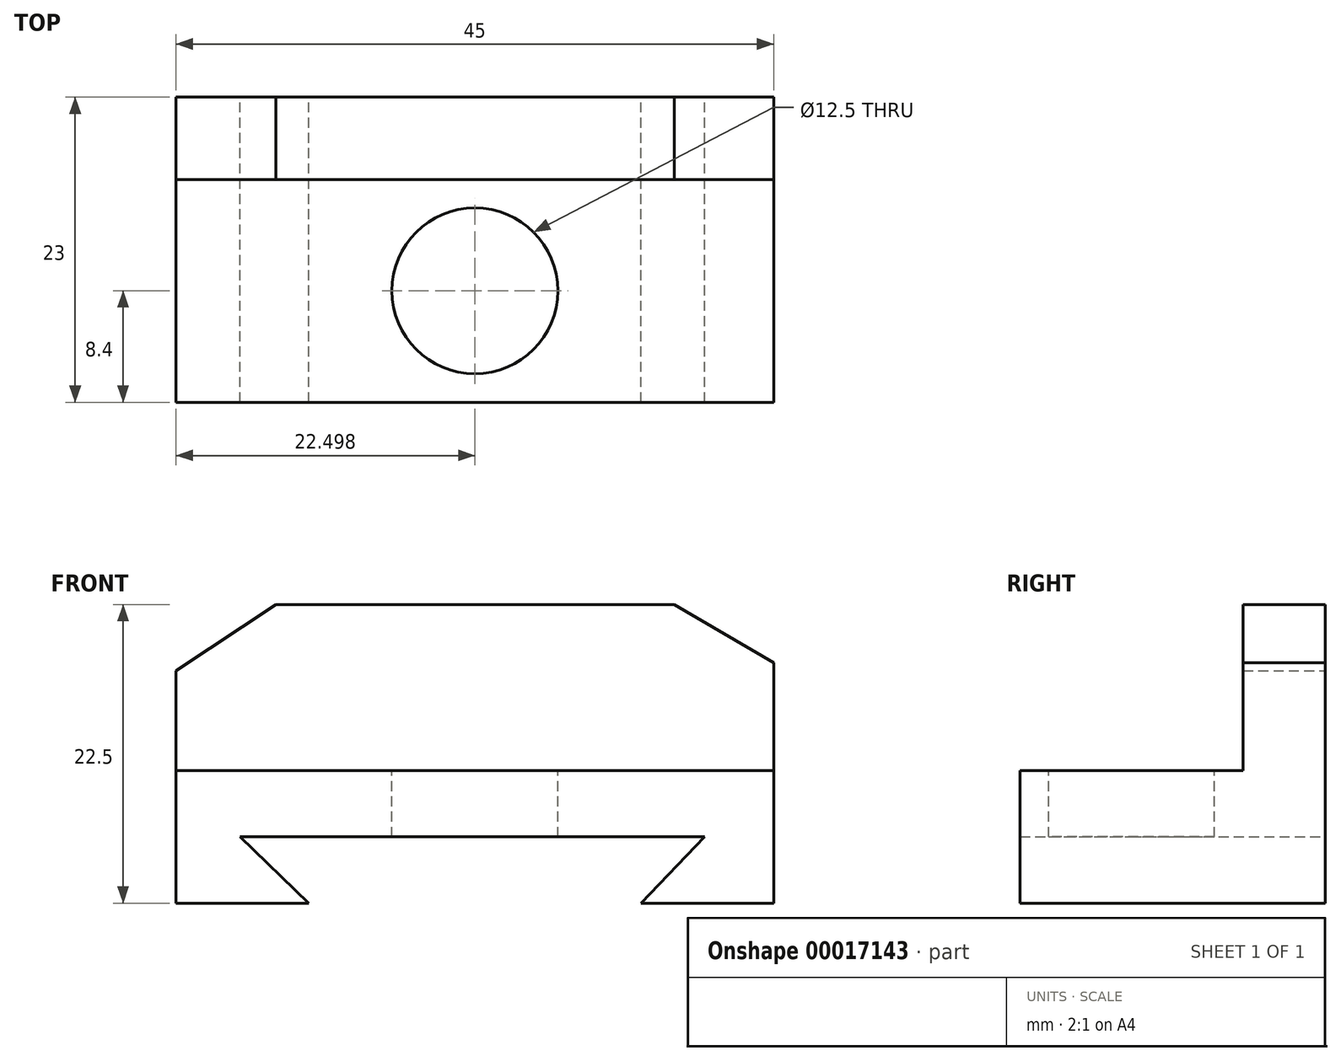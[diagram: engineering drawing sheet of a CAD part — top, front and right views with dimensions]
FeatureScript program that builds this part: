
annotation { "Feature Type Name" : "Feature", "Feature Type Description" : "" }
export const myFeature = defineFeature(function(context is Context, id is Id, definition is map)
    precondition{}
    {
        {
            var Q0;
            Q0=qCreatedBy(makeId("Front.planeOp"),FACE);
            var sketch = newSketch(context, id + "F0", { "sketchPlane" : qUnion([Q0])});
            skLineSegment(sketch, "E0", {"start": v(-23.08, -34) * mm, "end": v(-23.08, -24) * mm});
            skLineSegment(sketch, "E1", {"start": v(-23.08, -24) * mm, "end": v(-23.08, -16.5) * mm});
            skLineSegment(sketch, "E2", {"start": v(-23.08, -16.5) * mm, "end": v(-15.58, -11.5) * mm});
            skLineSegment(sketch, "E3", {"start": v(-15.58, -11.5) * mm, "end": v(14.42, -11.5) * mm});
            skLineSegment(sketch, "E4", {"start": v(21.92, -34) * mm, "end": v(21.92, -24) * mm});
            skLineSegment(sketch, "E5", {"start": v(21.92, -24) * mm, "end": v(21.92, -15.9) * mm});
            skLineSegment(sketch, "E6", {"start": v(-23.08, -24) * mm, "end": v(21.92, -24) * mm});
            skLineSegment(sketch, "E7", {"start": v(14.42, -11.5) * mm, "end": v(21.92, -15.9) * mm});
            skLineSegment(sketch, "E8", {"start": v(-23.08, -34) * mm, "end": v(-13.08, -34) * mm});
            skLineSegment(sketch, "E9", {"start": v(21.92, -34) * mm, "end": v(11.92, -34) * mm});
            skLineSegment(sketch, "E10", {"start": v(-13.08, -34) * mm, "end": v(-18.27, -29.01) * mm});
            skLineSegment(sketch, "E11", {"start": v(-18.27, -29.01) * mm, "end": v(16.73, -29.01) * mm});
            skLineSegment(sketch, "E12", {"start": v(11.92, -34) * mm, "end": v(16.73, -29.01) * mm});
            skSolve(sketch);
        }
        {
            var Q0;
            Q0=makeQuery(id+"F0.imprint","IMPRINT",FACE,{"disambiguationData":[TD([[makeQuery(id+"F0.imprint","IMPRINT",EDGE,{"derivedFrom":sQuery(id+"F0.wireOp",EDGE,"E0")}),-1.0]])]});
            extrude(context, id + "F1", {"entities" : qUnion([Q0]), "depth" : 23 * mm});
        }
        {
            var Q0;
            Q0 = qSketchRegion(id + "F0", true);
            extrude(context, id + "F2", {"entities" : qUnion([Q0]), "operationType" : NewBodyOperationType.ADD, "depth" : 6.2 * mm});
        }
        {
            var Q0;
            Q0=makeQuery(id+"F1.opExtrude","SWEPT_FACE",FACE,{"disambiguationData":[OSD([sQuery(id+"F0.wireOp",EDGE,"E6")])]});
            var sketch = newSketch(context, id + "F3", { "sketchPlane" : qUnion([Q0])});
            skCircle(sketch, "E13", {"center": v(-0.58, -14.6) * mm, "radius": 6.25 * mm});
            skSolve(sketch);
        }
        {
            var Q0;
            Q0 = qSketchRegion(id + "F3", true);
            extrude(context, id + "F4", {"entities" : qUnion([Q0]), "operationType" : NewBodyOperationType.REMOVE, "endBound" : BoundingType.THROUGH_ALL, "oppositeDirection" : true, "depth" : 25 * mm});
        }
    });
